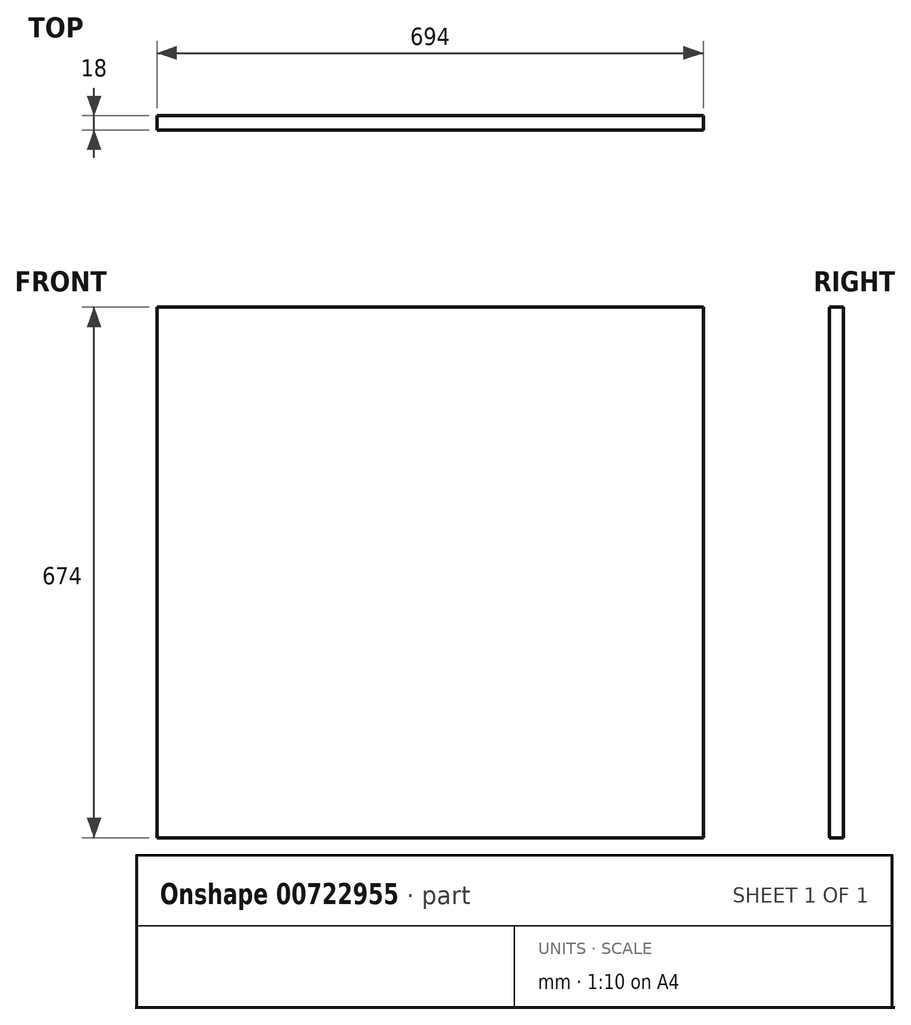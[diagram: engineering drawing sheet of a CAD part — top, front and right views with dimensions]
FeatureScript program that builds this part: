
annotation { "Feature Type Name" : "Feature", "Feature Type Description" : "" }
export const myFeature = defineFeature(function(context is Context, id is Id, definition is map)
    precondition{}
    {
        {
            var Q0;
            Q0=qCreatedBy(makeId("Front.planeOp"),FACE);
            var sketch = newSketch(context, id + "F0", { "sketchPlane" : qUnion([Q0])});
            skLineSegment(sketch, "E0.bottom", {"start": v(-347, 337) * mm, "end": v(347, 337) * mm});
            skLineSegment(sketch, "E0.top", {"start": v(-347, -337) * mm, "end": v(347, -337) * mm});
            skLineSegment(sketch, "E0.left", {"start": v(-347, 337) * mm, "end": v(-347, -337) * mm});
            skLineSegment(sketch, "E0.right", {"start": v(347, 337) * mm, "end": v(347, -337) * mm});
            skLineSegment(sketch, "E1", {"start": v(-347, 337) * mm, "end": v(347, -337) * mm, "construction": true});
            skLineSegment(sketch, "E2", {"start": v(347, 337) * mm, "end": v(-347, -337) * mm, "construction": true});
            skSolve(sketch);
        }
        {
            var Q0;
            Q0 = qSketchRegion(id + "F0", true);
            extrude(context, id + "F1", {"entities" : qUnion([Q0]), "depth" : 18 * mm, "offsetDistance" : 25 * mm});
        }
    });
